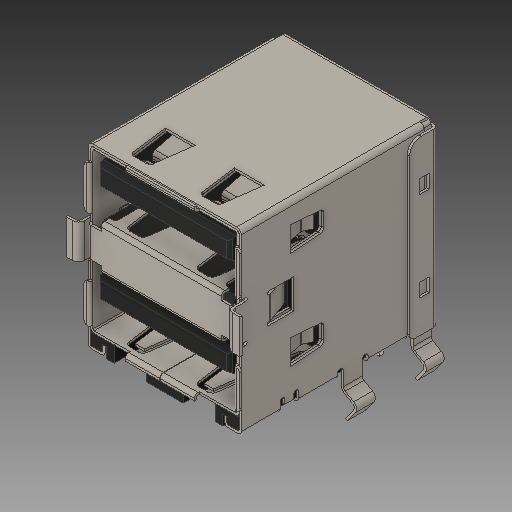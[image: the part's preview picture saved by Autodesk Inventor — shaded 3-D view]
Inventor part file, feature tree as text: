
AUTODESK INVENTOR PART (.ipt)
format: ipt  version: 2017 (Build 210142000, 142)  size: 1,051,648 bytes
history: native  units: in
note: dims shown in document units (in); Inventor stores cm internally (conversion verified against a paired STEP export)
features: other x3, sketch x1
ambient origin geometry x8: Origin, YZ Plane, XZ Plane, XY Plane, X Axis, Y Axis, Z Axis, Center Point
bodies: Solid1 (feature_tree), Solid2 (feature_tree), Solid3 (feature_tree), Solid4 (feature_tree)
feature tree (4):
  sketch  "Sketched Bend22"
  other  "Cut-Extrude5"
  other  "Cut-Extrude8"
  other  "Edge-Flange41"
